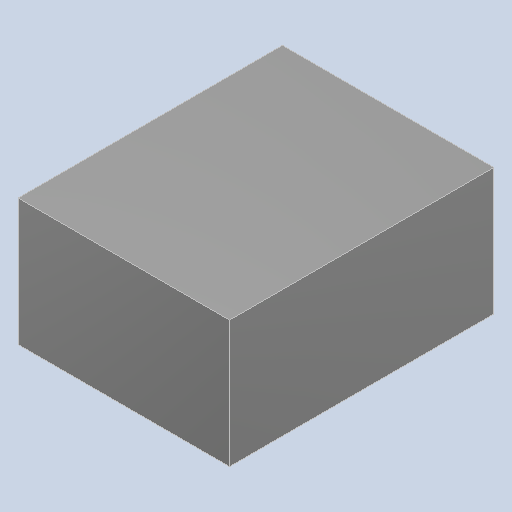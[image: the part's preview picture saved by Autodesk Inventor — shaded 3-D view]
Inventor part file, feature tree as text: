
AUTODESK INVENTOR PART (.ipt)
format: ipt  version: 2022 (Build 260153000, 153)  size: 87,040 bytes
history: imported  units: in
note: dims shown in document units (in); Inventor stores cm internally (conversion verified against a paired STEP export)
features: imported_body x1
ambient origin geometry x8: Origin, YZ Plane, XZ Plane, XY Plane, X Axis, Y Axis, Z Axis, Center Point
bodies: Solid1 (imported_parasolid)
feature tree (1):
  imported_body  NMx_Import_Brep_tag  [imported B-rep: ~6 faces, bbox_mm=[2.0, 1.2, 2.5]]
